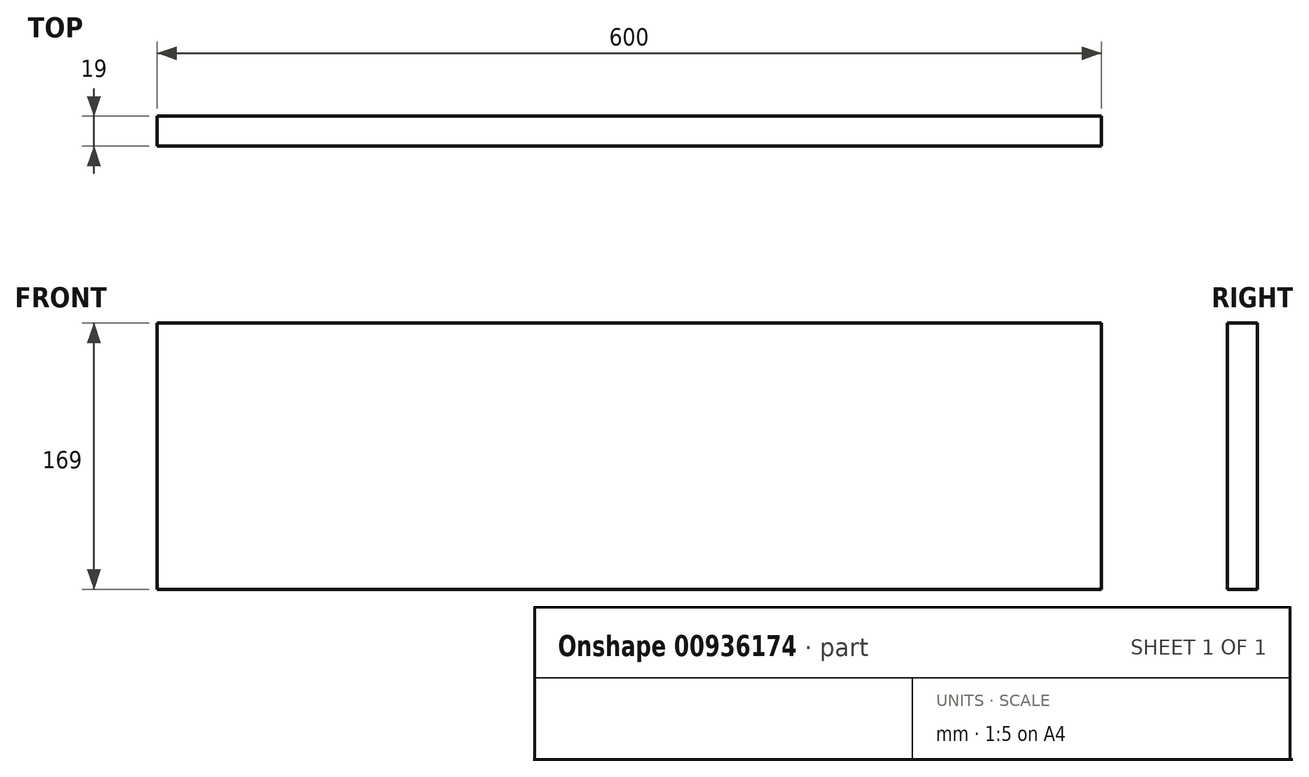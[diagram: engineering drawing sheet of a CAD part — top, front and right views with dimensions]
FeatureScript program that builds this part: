
annotation { "Feature Type Name" : "Feature", "Feature Type Description" : "" }
export const myFeature = defineFeature(function(context is Context, id is Id, definition is map)
    precondition{}
    {
        {
            var Q0;
            Q0=qCreatedBy(makeId("Front.planeOp"),FACE);
            var sketch = newSketch(context, id + "F0", { "sketchPlane" : qUnion([Q0])});
            skLineSegment(sketch, "E0.bottom", {"start": v(0, 0) * mm, "end": v(600, 0) * mm});
            skLineSegment(sketch, "E0.top", {"start": v(0, 169) * mm, "end": v(600, 169) * mm});
            skLineSegment(sketch, "E0.left", {"start": v(0, 0) * mm, "end": v(0, 169) * mm});
            skLineSegment(sketch, "E0.right", {"start": v(600, 0) * mm, "end": v(600, 169) * mm});
            skSolve(sketch);
        }
        {
            var Q0;
            Q0=makeQuery(id+"F0.imprint","IMPRINT",FACE,{"disambiguationData":[TD([[makeQuery(id+"F0.imprint","IMPRINT",EDGE,{"derivedFrom":sQuery(id+"F0.wireOp",EDGE,"E0.bottom")}),1.0]])]});
            extrude(context, id + "F1", {"entities" : qUnion([Q0]), "depth" : 19 * mm, "offsetDistance" : 25 * mm});
        }
    });
